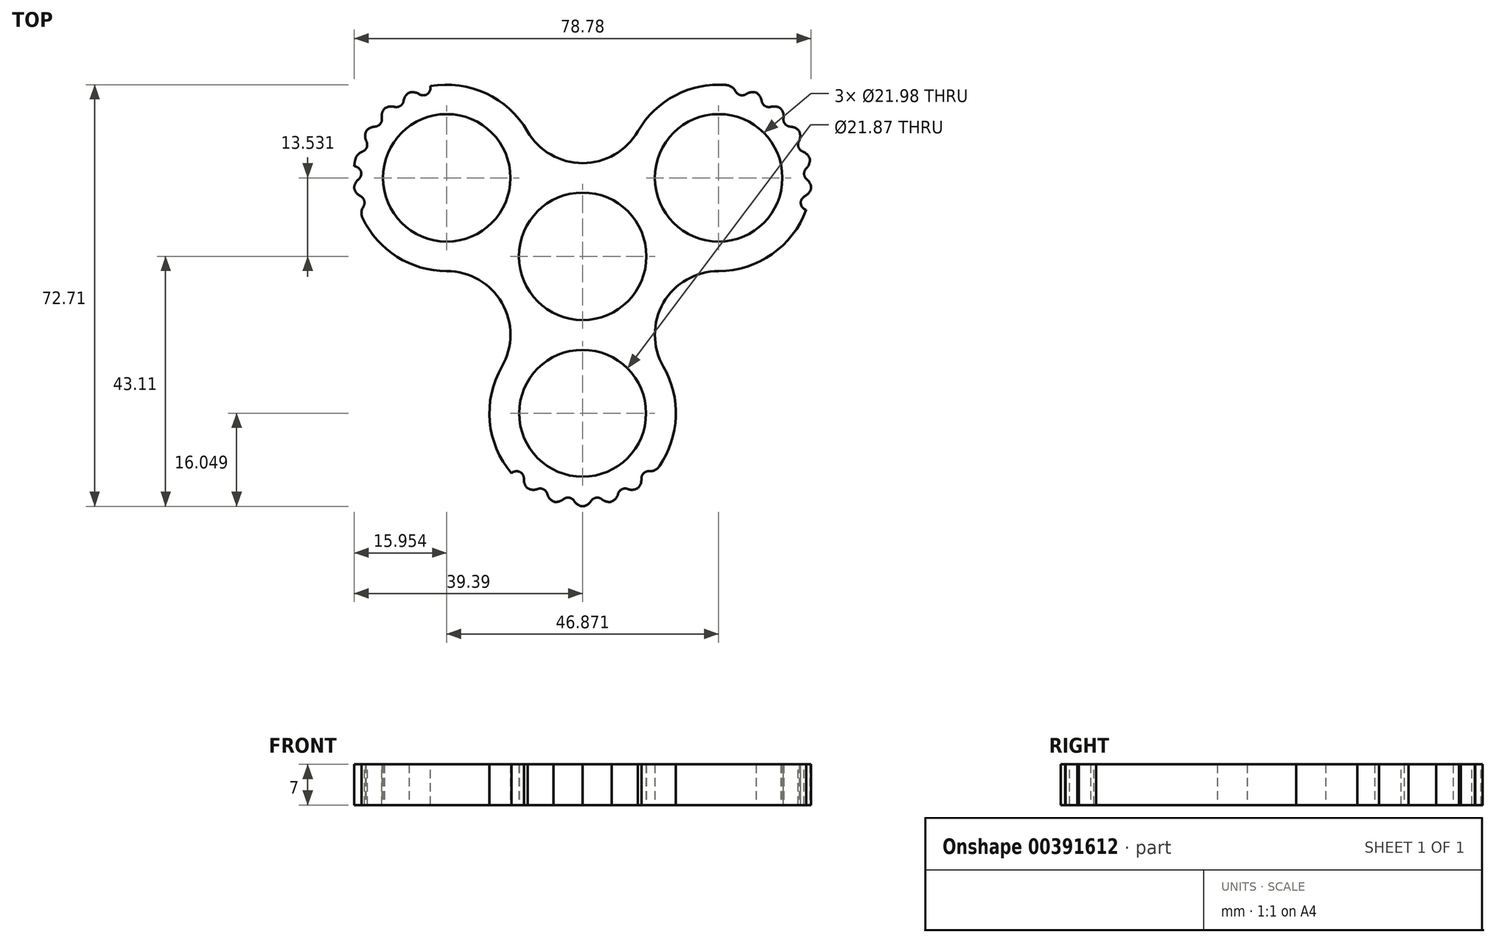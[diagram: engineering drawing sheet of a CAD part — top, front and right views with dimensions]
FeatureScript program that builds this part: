
annotation { "Feature Type Name" : "Feature", "Feature Type Description" : "" }
export const myFeature = defineFeature(function(context is Context, id is Id, definition is map)
    precondition{}
    {
        {
            var Q0;
            Q0=qCreatedBy(makeId("Top.planeOp"),FACE);
            var sketch = newSketch(context, id + "F0", { "sketchPlane" : qUnion([Q0])});
            skArc(sketch, "E0", {"start": v(0, 11) * mm, "mid": v(-5.5, -9.52) * mm, "end": v(9.52, 5.5) * mm, "construction": true});
            skLineSegment(sketch, "E1", {"start": v(0, 0) * mm, "end": v(92.12, 53.18) * mm, "construction": true});
            skLineSegment(sketch, "E2", {"start": v(0, 0) * mm, "end": v(-9.52, 5.5) * mm, "construction": true});
            skLineSegment(sketch, "E3", {"start": v(0, 0) * mm, "end": v(0, -70.87) * mm, "construction": true});
            skCircle(sketch, "E4", {"center": v(-23.44, 13.53) * mm, "radius": 11 * mm, "construction": true});
            skArc(sketch, "E5", {"start": v(13.92, 8.04) * mm, "mid": v(28.93, 4.01) * mm, "end": v(32.95, 19.03) * mm, "construction": true});
            skCircle(sketch, "E6", {"center": v(0, -27.06) * mm, "radius": 11 * mm, "construction": true});
            skLineSegment(sketch, "E7", {"start": v(0, 0) * mm, "end": v(-69.62, -40.2) * mm, "construction": true});
            skLineSegment(sketch, "E8", {"start": v(0, 0) * mm, "end": v(71.9, -41.52) * mm, "construction": true});
            skLineSegment(sketch, "E9", {"start": v(0, 0) * mm, "end": v(0, 11) * mm, "construction": true});
            skLineSegment(sketch, "E10", {"start": v(-23.44, 13.53) * mm, "end": v(-12.14, 33.1) * mm, "construction": true});
            skLineSegment(sketch, "E11", {"start": v(23.44, 13.53) * mm, "end": v(12.02, 33.3) * mm, "construction": true});
            skLineSegment(sketch, "E12", {"start": v(-37.35, 21.57) * mm, "end": v(-32.95, 19.03) * mm, "construction": true});
            skLineSegment(sketch, "E13", {"start": v(9.52, 5.5) * mm, "end": v(13.92, 8.04) * mm});
            skLineSegment(sketch, "E14", {"start": v(37.35, 21.57) * mm, "end": v(32.95, 19.03) * mm});
            skArc(sketch, "E15", {"start": v(-9.52, 5.5) * mm, "mid": v(-5.5, 9.52) * mm, "end": v(0, 11) * mm});
            skArc(sketch, "E16", {"start": v(-9.52, 21.57) * mm, "mid": v(-5.5, 17.54) * mm, "end": v(0, 16.07) * mm});
            skArc(sketch, "E17", {"start": v(-32.95, 19.03) * mm, "mid": v(-17.94, 23.05) * mm, "end": v(-13.92, 8.04) * mm});
            skLineSegment(sketch, "E18.trimOffspring", {"start": v(-37.35, 21.57) * mm, "end": v(-92.12, 53.18) * mm, "construction": true});
            skLineSegment(sketch, "E19.trimOffspring", {"start": v(-13.92, 8.04) * mm, "end": v(-32.95, 19.03) * mm, "construction": true});
            skArc(sketch, "E20", {"start": v(-9.52, 21.57) * mm, "mid": v(-23.44, 29.6) * mm, "end": v(-37.35, 21.57) * mm});
            skLineSegment(sketch, "E21", {"start": v(-37.35, 21.57) * mm, "end": v(-32.95, 19.03) * mm});
            skLineSegment(sketch, "E22", {"start": v(-13.92, 8.04) * mm, "end": v(-9.52, 5.5) * mm});
            skPoint(sketch, "E23.start.orphan", {"position": v(23.44, 29.6) * mm});
            skLineSegment(sketch, "E24.trimOffspring", {"start": v(0, 16.07) * mm, "end": v(0, 62.86) * mm, "construction": true});
            skLineSegment(sketch, "E25", {"start": v(0, 16.07) * mm, "end": v(0, 11) * mm});
            skLineSegment(sketch, "E26.MirrorCS", {"start": v(-13.92, -8.04) * mm, "end": v(-9.52, -5.5) * mm});
            skArc(sketch, "E27.MirrorCS", {"start": v(-23.44, -2.54) * mm, "mid": v(-17.94, -4.01) * mm, "end": v(-13.92, -8.04) * mm});
            skArc(sketch, "E28.MirrorCS", {"start": v(-23.44, -2.54) * mm, "mid": v(-37.35, 5.5) * mm, "end": v(-37.35, 21.57) * mm});
            skArc(sketch, "E29.MirrorCS", {"start": v(-9.52, 5.5) * mm, "mid": v(-11, 0) * mm, "end": v(-9.52, -5.5) * mm});
            skArc(sketch, "E30.MirrorCS", {"start": v(-32.95, 19.03) * mm, "mid": v(-28.93, 4.01) * mm, "end": v(-13.92, 8.04) * mm});
            skArc(sketch, "E31.MirrorCS", {"start": v(23.44, -2.54) * mm, "mid": v(37.35, 5.5) * mm, "end": v(37.35, 21.57) * mm});
            skLineSegment(sketch, "E32.MirrorCS", {"start": v(13.92, 8.04) * mm, "end": v(9.52, 5.5) * mm});
            skArc(sketch, "E33.MirrorCS", {"start": v(32.95, 19.03) * mm, "mid": v(17.94, 23.05) * mm, "end": v(13.92, 8.04) * mm});
            skArc(sketch, "E34.MirrorCS", {"start": v(32.95, 19.03) * mm, "mid": v(28.93, 4.01) * mm, "end": v(13.92, 8.04) * mm});
            skLineSegment(sketch, "E35.MirrorCS", {"start": v(13.92, -8.04) * mm, "end": v(9.52, -5.5) * mm});
            skArc(sketch, "E36.MirrorCS", {"start": v(23.44, -2.54) * mm, "mid": v(17.94, -4.01) * mm, "end": v(13.92, -8.04) * mm});
            skLineSegment(sketch, "E37.MirrorCS", {"start": v(37.35, 21.57) * mm, "end": v(32.95, 19.03) * mm, "construction": true});
            skArc(sketch, "E38.MirrorCS", {"start": v(9.52, 5.5) * mm, "mid": v(11, 0) * mm, "end": v(9.52, -5.5) * mm});
            skArc(sketch, "E39.MirrorCS", {"start": v(9.52, 21.57) * mm, "mid": v(23.44, 29.6) * mm, "end": v(37.35, 21.57) * mm});
            skLineSegment(sketch, "E40.MirrorCS", {"start": v(23.44, 13.53) * mm, "end": v(12.14, 33.1) * mm, "construction": true});
            skLineSegment(sketch, "E41.MirrorCS", {"start": v(0, 0) * mm, "end": v(9.52, 5.5) * mm, "construction": true});
            skArc(sketch, "E42.MirrorCS", {"start": v(9.52, 5.5) * mm, "mid": v(5.5, 9.52) * mm, "end": v(0, 11) * mm});
            skArc(sketch, "E43.MirrorCS", {"start": v(9.52, 21.57) * mm, "mid": v(5.5, 17.54) * mm, "end": v(0, 16.07) * mm});
            skCircle(sketch, "E44.MirrorC", {"center": v(23.44, 13.53) * mm, "radius": 11 * mm, "construction": true});
            skLineSegment(sketch, "E45.MirrorCS", {"start": v(13.92, 8.04) * mm, "end": v(32.95, 19.03) * mm, "construction": true});
            skArc(sketch, "E46", {"start": v(-9.52, -5.5) * mm, "mid": v(0, -11) * mm, "end": v(9.52, -5.5) * mm});
            skArc(sketch, "E47.MirrorCS", {"start": v(-13.92, -19.03) * mm, "mid": v(-12.45, -13.53) * mm, "end": v(-13.92, -8.04) * mm});
            skArc(sketch, "E48.MirrorCS", {"start": v(-13.92, -19.03) * mm, "mid": v(-13.92, -35.1) * mm, "end": v(0, -43.13) * mm});
            skArc(sketch, "E49.MirrorCS", {"start": v(13.92, -19.03) * mm, "mid": v(12.45, -13.53) * mm, "end": v(13.92, -8.04) * mm});
            skArc(sketch, "E50.MirrorCS", {"start": v(13.92, -19.03) * mm, "mid": v(13.92, -35.1) * mm, "end": v(0, -43.13) * mm});
            skCircle(sketch, "E51", {"center": v(0, -27.06) * mm, "radius": 10.94 * mm});
            skSolve(sketch);
        }
        {
            var Q0;
            Q0=qSketchRegion(id+"F0",true);
            extrude(context, id + "F1", {"entities" : qUnion([Q0]), "depth" : 7 * mm});
        }
        {
            var Q0;
            Q0=makeQuery(id+"F1.opExtrude","CAP_FACE",FACE,{"disambiguationData":[OSD([sQuery(id+"F0.wireOp",EDGE,"E15"),sQuery(id+"F0.wireOp",EDGE,"E16"),sQuery(id+"F0.wireOp",EDGE,"E17"),sQuery(id+"F0.wireOp",EDGE,"E20"),sQuery(id+"F0.wireOp",EDGE,"E27.MirrorCS"),sQuery(id+"F0.wireOp",EDGE,"E29.MirrorCS"),sQuery(id+"F0.wireOp",EDGE,"E30.MirrorCS"),sQuery(id+"F0.wireOp",EDGE,"E28.MirrorCS"),sQuery(id+"F0.wireOp",EDGE,"E33.MirrorCS"),sQuery(id+"F0.wireOp",EDGE,"E34.MirrorCS"),sQuery(id+"F0.wireOp",EDGE,"E31.MirrorCS"),sQuery(id+"F0.wireOp",EDGE,"E36.MirrorCS"),sQuery(id+"F0.wireOp",EDGE,"E38.MirrorCS"),sQuery(id+"F0.wireOp",EDGE,"E39.MirrorCS"),sQuery(id+"F0.wireOp",EDGE,"E42.MirrorCS"),sQuery(id+"F0.wireOp",EDGE,"E43.MirrorCS"),sQuery(id+"F0.wireOp",EDGE,"E46"),sQuery(id+"F0.wireOp",EDGE,"E47.MirrorCS"),sQuery(id+"F0.wireOp",EDGE,"E48.MirrorCS"),sQuery(id+"F0.wireOp",EDGE,"E49.MirrorCS"),sQuery(id+"F0.wireOp",EDGE,"E50.MirrorCS"),sQuery(id+"F0.wireOp",EDGE,"E51")])],"isStart":false});
            var sketch = newSketch(context, id + "F2", { "sketchPlane" : qUnion([Q0])});
            skArc(sketch, "E52", {"start": v(-36.68, 22.64) * mm, "mid": v(-34.89, 22.83) * mm, "end": v(-35.07, 24.61) * mm});
            skArc(sketch, "E53", {"start": v(-38.85, 18.07) * mm, "mid": v(-37.21, 18.8) * mm, "end": v(-37.94, 20.44) * mm});
            skArc(sketch, "E54", {"start": v(-36.68, 22.64) * mm, "mid": v(-35.91, 23.66) * mm, "end": v(-35.07, 24.61) * mm});
            skArc(sketch, "E55", {"start": v(-38.85, 18.07) * mm, "mid": v(-38.45, 19.27) * mm, "end": v(-37.94, 20.44) * mm});
            skArc(sketch, "E56", {"start": v(-39.5, 12.99) * mm, "mid": v(-38.17, 14.2) * mm, "end": v(-39.38, 15.53) * mm});
            skArc(sketch, "E57", {"start": v(-33.18, 26.3) * mm, "mid": v(-31.43, 25.93) * mm, "end": v(-31.05, 27.68) * mm});
            skArc(sketch, "E58", {"start": v(-33.18, 26.3) * mm, "mid": v(-32.14, 27.04) * mm, "end": v(-31.05, 27.68) * mm});
            skArc(sketch, "E59", {"start": v(-39.5, 12.99) * mm, "mid": v(-39.49, 14.26) * mm, "end": v(-39.38, 15.53) * mm});
            skArc(sketch, "E60", {"start": v(-38.53, 8.02) * mm, "mid": v(-37.65, 9.58) * mm, "end": v(-39.21, 10.47) * mm});
            skArc(sketch, "E61", {"start": v(-28.72, 28.7) * mm, "mid": v(-27.17, 27.8) * mm, "end": v(-26.27, 29.35) * mm});
            skArc(sketch, "E62", {"start": v(-28.72, 28.7) * mm, "mid": v(-27.5, 29.08) * mm, "end": v(-26.27, 29.35) * mm});
            skArc(sketch, "E63", {"start": v(-38.53, 8.02) * mm, "mid": v(-38.92, 9.23) * mm, "end": v(-39.21, 10.47) * mm});
            skLineSegment(sketch, "E64", {"start": v(0, 53.35) * mm, "end": v(0, -27.06) * mm, "construction": true});
            skArc(sketch, "E65.MirrorCS", {"start": v(28.72, 28.7) * mm, "mid": v(27.17, 27.8) * mm, "end": v(26.27, 29.35) * mm});
            skArc(sketch, "E66.MirrorCS", {"start": v(28.72, 28.7) * mm, "mid": v(27.5, 29.08) * mm, "end": v(26.27, 29.35) * mm});
            skArc(sketch, "E67.MirrorCS", {"start": v(33.18, 26.3) * mm, "mid": v(31.43, 25.93) * mm, "end": v(31.05, 27.68) * mm});
            skArc(sketch, "E68.MirrorCS", {"start": v(33.18, 26.3) * mm, "mid": v(32.14, 27.04) * mm, "end": v(31.05, 27.68) * mm});
            skArc(sketch, "E69.MirrorCS", {"start": v(36.68, 22.64) * mm, "mid": v(34.89, 22.83) * mm, "end": v(35.07, 24.61) * mm});
            skArc(sketch, "E70.MirrorCS", {"start": v(38.85, 18.07) * mm, "mid": v(37.21, 18.8) * mm, "end": v(37.94, 20.44) * mm});
            skArc(sketch, "E71.MirrorCS", {"start": v(39.5, 12.99) * mm, "mid": v(38.17, 14.2) * mm, "end": v(39.38, 15.53) * mm});
            skArc(sketch, "E72.MirrorCS", {"start": v(38.53, 8.02) * mm, "mid": v(37.65, 9.58) * mm, "end": v(39.21, 10.47) * mm});
            skArc(sketch, "E73.MirrorCS", {"start": v(36.68, 22.64) * mm, "mid": v(35.91, 23.66) * mm, "end": v(35.07, 24.61) * mm});
            skArc(sketch, "E74.MirrorCS", {"start": v(38.85, 18.07) * mm, "mid": v(38.45, 19.27) * mm, "end": v(37.94, 20.44) * mm});
            skArc(sketch, "E75.MirrorCS", {"start": v(39.5, 12.99) * mm, "mid": v(39.49, 14.26) * mm, "end": v(39.38, 15.53) * mm});
            skArc(sketch, "E76.MirrorCS", {"start": v(38.53, 8.02) * mm, "mid": v(38.92, 9.23) * mm, "end": v(39.21, 10.47) * mm});
            skArc(sketch, "E77", {"start": v(3.78, -42.68) * mm, "mid": v(2.32, -41.63) * mm, "end": v(1.27, -43.08) * mm});
            skArc(sketch, "E78", {"start": v(8.45, -40.73) * mm, "mid": v(6.74, -40.18) * mm, "end": v(6.2, -41.9) * mm});
            skArc(sketch, "E79", {"start": v(12.28, -37.42) * mm, "mid": v(10.49, -37.43) * mm, "end": v(10.5, -39.23) * mm});
            skArc(sketch, "E80", {"start": v(-1.27, -43.08) * mm, "mid": v(-2.32, -41.63) * mm, "end": v(-3.78, -42.68) * mm});
            skArc(sketch, "E81", {"start": v(-6.2, -41.9) * mm, "mid": v(-6.74, -40.18) * mm, "end": v(-8.45, -40.73) * mm});
            skArc(sketch, "E82", {"start": v(-10.5, -39.23) * mm, "mid": v(-10.49, -37.43) * mm, "end": v(-12.28, -37.42) * mm});
            skArc(sketch, "E83", {"start": v(12.28, -37.42) * mm, "mid": v(11.43, -38.36) * mm, "end": v(10.5, -39.23) * mm});
            skArc(sketch, "E84", {"start": v(8.45, -40.73) * mm, "mid": v(7.34, -41.36) * mm, "end": v(6.2, -41.9) * mm});
            skArc(sketch, "E85", {"start": v(3.78, -42.68) * mm, "mid": v(2.53, -42.93) * mm, "end": v(1.27, -43.08) * mm});
            skArc(sketch, "E86", {"start": v(-1.27, -43.08) * mm, "mid": v(-2.53, -42.93) * mm, "end": v(-3.78, -42.68) * mm});
            skArc(sketch, "E87", {"start": v(-6.2, -41.9) * mm, "mid": v(-7.34, -41.36) * mm, "end": v(-8.45, -40.73) * mm});
            skArc(sketch, "E88", {"start": v(-10.5, -39.23) * mm, "mid": v(-11.43, -38.36) * mm, "end": v(-12.28, -37.42) * mm});
            skSolve(sketch);
        }
        {
            var Q0;
            Q0=qSketchRegion(id+"F2",true);
            extrude(context, id + "F3", {"entities" : qUnion([Q0]), "operationType" : NewBodyOperationType.REMOVE, "endBound" : BoundingType.THROUGH_ALL, "oppositeDirection" : true, "depth" : 25.4 * mm});
        }
        {
            var Q0;
            {var subQ0=sQuery(id+"F2.wireOp",EDGE,"E84");var subQ1=sQuery(id+"F2.wireOp",EDGE,"E78");var subQ2=sQuery(id+"F0.wireOp",EDGE,"E50.MirrorCS");var subQ3=sQuery(id+"F0.wireOp",EDGE,"E48.MirrorCS");Q0=makeQuery(id+"F3.boolean.opBoolean","COPY",EDGE,{"derivedFrom":makeQuery(id+"F3.opExtrude","SWEPT_EDGE",EDGE,{"disambiguationData":[OSD([subQ3,subQ2,subQ1,subQ0]),TDD([makeQuery(id+"F2.imprint","INTERSECT",VERTEX,{"disambiguationData":[OD(0.0)],"derivedFrom":[makeQuery(id+"F1.opExtrude","CAP_EDGE",EDGE,{"disambiguationData":[OSD([subQ3,subQ2])],"isStart":false}),subQ1,subQ0]})])]})});}
            var Q1;
            {var subQ0=sQuery(id+"F2.wireOp",EDGE,"E83");var subQ1=sQuery(id+"F2.wireOp",EDGE,"E79");var subQ2=sQuery(id+"F0.wireOp",EDGE,"E50.MirrorCS");var subQ3=sQuery(id+"F0.wireOp",EDGE,"E48.MirrorCS");Q1=makeQuery(id+"F3.boolean.opBoolean","COPY",EDGE,{"derivedFrom":makeQuery(id+"F3.opExtrude","SWEPT_EDGE",EDGE,{"disambiguationData":[OSD([subQ3,subQ2,subQ1,subQ0]),TDD([makeQuery(id+"F2.imprint","INTERSECT",VERTEX,{"disambiguationData":[OD(1.0)],"derivedFrom":[makeQuery(id+"F1.opExtrude","CAP_EDGE",EDGE,{"disambiguationData":[OSD([subQ3,subQ2])],"isStart":false}),subQ1,subQ0]})])]})});}
            var Q2;
            {var subQ0=sQuery(id+"F2.wireOp",EDGE,"E85");var subQ1=sQuery(id+"F2.wireOp",EDGE,"E77");var subQ2=sQuery(id+"F0.wireOp",EDGE,"E50.MirrorCS");var subQ3=sQuery(id+"F0.wireOp",EDGE,"E48.MirrorCS");Q2=makeQuery(id+"F3.boolean.opBoolean","COPY",EDGE,{"derivedFrom":makeQuery(id+"F3.opExtrude","SWEPT_EDGE",EDGE,{"disambiguationData":[OSD([subQ3,subQ2,subQ1,subQ0]),TDD([makeQuery(id+"F2.imprint","INTERSECT",VERTEX,{"disambiguationData":[OD(0.0)],"derivedFrom":[makeQuery(id+"F1.opExtrude","CAP_EDGE",EDGE,{"disambiguationData":[OSD([subQ3,subQ2])],"isStart":false}),subQ1,subQ0]})])]})});}
            var Q3;
            {var subQ0=sQuery(id+"F2.wireOp",EDGE,"E84");var subQ1=sQuery(id+"F2.wireOp",EDGE,"E78");var subQ2=sQuery(id+"F0.wireOp",EDGE,"E50.MirrorCS");var subQ3=sQuery(id+"F0.wireOp",EDGE,"E48.MirrorCS");Q3=makeQuery(id+"F3.boolean.opBoolean","COPY",EDGE,{"derivedFrom":makeQuery(id+"F3.opExtrude","SWEPT_EDGE",EDGE,{"disambiguationData":[OSD([subQ3,subQ2,subQ1,subQ0]),TDD([makeQuery(id+"F2.imprint","INTERSECT",VERTEX,{"disambiguationData":[OD(1.0)],"derivedFrom":[makeQuery(id+"F1.opExtrude","CAP_EDGE",EDGE,{"disambiguationData":[OSD([subQ3,subQ2])],"isStart":false}),subQ1,subQ0]})])]})});}
            var Q4;
            {var subQ0=sQuery(id+"F2.wireOp",EDGE,"E85");var subQ1=sQuery(id+"F2.wireOp",EDGE,"E77");var subQ2=sQuery(id+"F0.wireOp",EDGE,"E50.MirrorCS");var subQ3=sQuery(id+"F0.wireOp",EDGE,"E48.MirrorCS");Q4=makeQuery(id+"F3.boolean.opBoolean","COPY",EDGE,{"derivedFrom":makeQuery(id+"F3.opExtrude","SWEPT_EDGE",EDGE,{"disambiguationData":[OSD([subQ3,subQ2,subQ1,subQ0]),TDD([makeQuery(id+"F2.imprint","INTERSECT",VERTEX,{"disambiguationData":[OD(1.0)],"derivedFrom":[makeQuery(id+"F1.opExtrude","CAP_EDGE",EDGE,{"disambiguationData":[OSD([subQ3,subQ2])],"isStart":false}),subQ1,subQ0]})])]})});}
            var Q5;
            {var subQ0=sQuery(id+"F2.wireOp",EDGE,"E86");var subQ1=sQuery(id+"F2.wireOp",EDGE,"E80");var subQ2=sQuery(id+"F0.wireOp",EDGE,"E50.MirrorCS");var subQ3=sQuery(id+"F0.wireOp",EDGE,"E48.MirrorCS");Q5=makeQuery(id+"F3.boolean.opBoolean","COPY",EDGE,{"derivedFrom":makeQuery(id+"F3.opExtrude","SWEPT_EDGE",EDGE,{"disambiguationData":[OSD([subQ3,subQ2,subQ1,subQ0]),TDD([makeQuery(id+"F2.imprint","INTERSECT",VERTEX,{"disambiguationData":[OD(0.0)],"derivedFrom":[makeQuery(id+"F1.opExtrude","CAP_EDGE",EDGE,{"disambiguationData":[OSD([subQ3,subQ2])],"isStart":false}),subQ1,subQ0]})])]})});}
            var Q6;
            {var subQ0=sQuery(id+"F2.wireOp",EDGE,"E86");var subQ1=sQuery(id+"F2.wireOp",EDGE,"E80");var subQ2=sQuery(id+"F0.wireOp",EDGE,"E50.MirrorCS");var subQ3=sQuery(id+"F0.wireOp",EDGE,"E48.MirrorCS");Q6=makeQuery(id+"F3.boolean.opBoolean","COPY",EDGE,{"derivedFrom":makeQuery(id+"F3.opExtrude","SWEPT_EDGE",EDGE,{"disambiguationData":[OSD([subQ3,subQ2,subQ1,subQ0]),TDD([makeQuery(id+"F2.imprint","INTERSECT",VERTEX,{"disambiguationData":[OD(1.0)],"derivedFrom":[makeQuery(id+"F1.opExtrude","CAP_EDGE",EDGE,{"disambiguationData":[OSD([subQ3,subQ2])],"isStart":false}),subQ1,subQ0]})])]})});}
            var Q7;
            {var subQ0=sQuery(id+"F2.wireOp",EDGE,"E87");var subQ1=sQuery(id+"F2.wireOp",EDGE,"E81");var subQ2=sQuery(id+"F0.wireOp",EDGE,"E50.MirrorCS");var subQ3=sQuery(id+"F0.wireOp",EDGE,"E48.MirrorCS");Q7=makeQuery(id+"F3.boolean.opBoolean","COPY",EDGE,{"derivedFrom":makeQuery(id+"F3.opExtrude","SWEPT_EDGE",EDGE,{"disambiguationData":[OSD([subQ3,subQ2,subQ1,subQ0]),TDD([makeQuery(id+"F2.imprint","INTERSECT",VERTEX,{"disambiguationData":[OD(0.0)],"derivedFrom":[makeQuery(id+"F1.opExtrude","CAP_EDGE",EDGE,{"disambiguationData":[OSD([subQ3,subQ2])],"isStart":false}),subQ1,subQ0]})])]})});}
            var Q8;
            {var subQ0=sQuery(id+"F2.wireOp",EDGE,"E87");var subQ1=sQuery(id+"F2.wireOp",EDGE,"E81");var subQ2=sQuery(id+"F0.wireOp",EDGE,"E50.MirrorCS");var subQ3=sQuery(id+"F0.wireOp",EDGE,"E48.MirrorCS");Q8=makeQuery(id+"F3.boolean.opBoolean","COPY",EDGE,{"derivedFrom":makeQuery(id+"F3.opExtrude","SWEPT_EDGE",EDGE,{"disambiguationData":[OSD([subQ3,subQ2,subQ1,subQ0]),TDD([makeQuery(id+"F2.imprint","INTERSECT",VERTEX,{"disambiguationData":[OD(1.0)],"derivedFrom":[makeQuery(id+"F1.opExtrude","CAP_EDGE",EDGE,{"disambiguationData":[OSD([subQ3,subQ2])],"isStart":false}),subQ1,subQ0]})])]})});}
            var Q9;
            {var subQ0=sQuery(id+"F2.wireOp",EDGE,"E88");var subQ1=sQuery(id+"F2.wireOp",EDGE,"E82");var subQ2=sQuery(id+"F0.wireOp",EDGE,"E50.MirrorCS");var subQ3=sQuery(id+"F0.wireOp",EDGE,"E48.MirrorCS");Q9=makeQuery(id+"F3.boolean.opBoolean","COPY",EDGE,{"derivedFrom":makeQuery(id+"F3.opExtrude","SWEPT_EDGE",EDGE,{"disambiguationData":[OSD([subQ3,subQ2,subQ1,subQ0]),TDD([makeQuery(id+"F2.imprint","INTERSECT",VERTEX,{"disambiguationData":[OD(0.0)],"derivedFrom":[makeQuery(id+"F1.opExtrude","CAP_EDGE",EDGE,{"disambiguationData":[OSD([subQ3,subQ2])],"isStart":false}),subQ1,subQ0]})])]})});}
            var Q10;
            {var subQ0=sQuery(id+"F2.wireOp",EDGE,"E62");var subQ1=sQuery(id+"F2.wireOp",EDGE,"E61");var subQ2=sQuery(id+"F0.wireOp",EDGE,"E28.MirrorCS");var subQ3=sQuery(id+"F0.wireOp",EDGE,"E20");Q10=makeQuery(id+"F3.boolean.opBoolean","COPY",EDGE,{"derivedFrom":makeQuery(id+"F3.opExtrude","SWEPT_EDGE",EDGE,{"disambiguationData":[OSD([subQ3,subQ2,subQ1,subQ0]),TDD([makeQuery(id+"F2.imprint","INTERSECT",VERTEX,{"disambiguationData":[OD(0.0)],"derivedFrom":[makeQuery(id+"F1.opExtrude","CAP_EDGE",EDGE,{"disambiguationData":[OSD([subQ3,subQ2])],"isStart":false}),subQ1,subQ0]})])]})});}
            var Q11;
            {var subQ0=sQuery(id+"F2.wireOp",EDGE,"E58");var subQ1=sQuery(id+"F2.wireOp",EDGE,"E57");var subQ2=sQuery(id+"F0.wireOp",EDGE,"E28.MirrorCS");var subQ3=sQuery(id+"F0.wireOp",EDGE,"E20");Q11=makeQuery(id+"F3.boolean.opBoolean","COPY",EDGE,{"derivedFrom":makeQuery(id+"F3.opExtrude","SWEPT_EDGE",EDGE,{"disambiguationData":[OSD([subQ3,subQ2,subQ1,subQ0]),TDD([makeQuery(id+"F2.imprint","INTERSECT",VERTEX,{"disambiguationData":[OD(1.0)],"derivedFrom":[makeQuery(id+"F1.opExtrude","CAP_EDGE",EDGE,{"disambiguationData":[OSD([subQ3,subQ2])],"isStart":false}),subQ1,subQ0]})])]})});}
            var Q12;
            {var subQ0=sQuery(id+"F2.wireOp",EDGE,"E58");var subQ1=sQuery(id+"F2.wireOp",EDGE,"E57");var subQ2=sQuery(id+"F0.wireOp",EDGE,"E28.MirrorCS");var subQ3=sQuery(id+"F0.wireOp",EDGE,"E20");Q12=makeQuery(id+"F3.boolean.opBoolean","COPY",EDGE,{"derivedFrom":makeQuery(id+"F3.opExtrude","SWEPT_EDGE",EDGE,{"disambiguationData":[OSD([subQ3,subQ2,subQ1,subQ0]),TDD([makeQuery(id+"F2.imprint","INTERSECT",VERTEX,{"disambiguationData":[OD(0.0)],"derivedFrom":[makeQuery(id+"F1.opExtrude","CAP_EDGE",EDGE,{"disambiguationData":[OSD([subQ3,subQ2])],"isStart":false}),subQ1,subQ0]})])]})});}
            var Q13;
            {var subQ0=sQuery(id+"F2.wireOp",EDGE,"E54");var subQ1=sQuery(id+"F2.wireOp",EDGE,"E52");var subQ2=sQuery(id+"F0.wireOp",EDGE,"E28.MirrorCS");var subQ3=sQuery(id+"F0.wireOp",EDGE,"E20");Q13=makeQuery(id+"F3.boolean.opBoolean","COPY",EDGE,{"derivedFrom":makeQuery(id+"F3.opExtrude","SWEPT_EDGE",EDGE,{"disambiguationData":[OSD([subQ3,subQ2,subQ1,subQ0]),TDD([makeQuery(id+"F2.imprint","INTERSECT",VERTEX,{"disambiguationData":[OD(1.0)],"derivedFrom":[makeQuery(id+"F1.opExtrude","CAP_EDGE",EDGE,{"disambiguationData":[OSD([subQ3,subQ2])],"isStart":false}),subQ1,subQ0]})])]})});}
            var Q14;
            {var subQ0=sQuery(id+"F2.wireOp",EDGE,"E54");var subQ1=sQuery(id+"F2.wireOp",EDGE,"E52");var subQ2=sQuery(id+"F0.wireOp",EDGE,"E28.MirrorCS");var subQ3=sQuery(id+"F0.wireOp",EDGE,"E20");Q14=makeQuery(id+"F3.boolean.opBoolean","COPY",EDGE,{"derivedFrom":makeQuery(id+"F3.opExtrude","SWEPT_EDGE",EDGE,{"disambiguationData":[OSD([subQ3,subQ2,subQ1,subQ0]),TDD([makeQuery(id+"F2.imprint","INTERSECT",VERTEX,{"disambiguationData":[OD(0.0)],"derivedFrom":[makeQuery(id+"F1.opExtrude","CAP_EDGE",EDGE,{"disambiguationData":[OSD([subQ3,subQ2])],"isStart":false}),subQ1,subQ0]})])]})});}
            var Q15;
            {var subQ0=sQuery(id+"F2.wireOp",EDGE,"E55");var subQ1=sQuery(id+"F2.wireOp",EDGE,"E53");var subQ2=sQuery(id+"F0.wireOp",EDGE,"E28.MirrorCS");var subQ3=sQuery(id+"F0.wireOp",EDGE,"E20");Q15=makeQuery(id+"F3.boolean.opBoolean","COPY",EDGE,{"derivedFrom":makeQuery(id+"F3.opExtrude","SWEPT_EDGE",EDGE,{"disambiguationData":[OSD([subQ3,subQ2,subQ1,subQ0]),TDD([makeQuery(id+"F2.imprint","INTERSECT",VERTEX,{"disambiguationData":[OD(1.0)],"derivedFrom":[makeQuery(id+"F1.opExtrude","CAP_EDGE",EDGE,{"disambiguationData":[OSD([subQ3,subQ2])],"isStart":false}),subQ1,subQ0]})])]})});}
            var Q16;
            {var subQ0=sQuery(id+"F2.wireOp",EDGE,"E55");var subQ1=sQuery(id+"F2.wireOp",EDGE,"E53");var subQ2=sQuery(id+"F0.wireOp",EDGE,"E28.MirrorCS");var subQ3=sQuery(id+"F0.wireOp",EDGE,"E20");Q16=makeQuery(id+"F3.boolean.opBoolean","COPY",EDGE,{"derivedFrom":makeQuery(id+"F3.opExtrude","SWEPT_EDGE",EDGE,{"disambiguationData":[OSD([subQ3,subQ2,subQ1,subQ0]),TDD([makeQuery(id+"F2.imprint","INTERSECT",VERTEX,{"disambiguationData":[OD(0.0)],"derivedFrom":[makeQuery(id+"F1.opExtrude","CAP_EDGE",EDGE,{"disambiguationData":[OSD([subQ3,subQ2])],"isStart":false}),subQ1,subQ0]})])]})});}
            var Q17;
            {var subQ0=sQuery(id+"F2.wireOp",EDGE,"E59");var subQ1=sQuery(id+"F2.wireOp",EDGE,"E56");var subQ2=sQuery(id+"F0.wireOp",EDGE,"E28.MirrorCS");var subQ3=sQuery(id+"F0.wireOp",EDGE,"E20");Q17=makeQuery(id+"F3.boolean.opBoolean","COPY",EDGE,{"derivedFrom":makeQuery(id+"F3.opExtrude","SWEPT_EDGE",EDGE,{"disambiguationData":[OSD([subQ3,subQ2,subQ1,subQ0]),TDD([makeQuery(id+"F2.imprint","INTERSECT",VERTEX,{"disambiguationData":[OD(0.0)],"derivedFrom":[makeQuery(id+"F1.opExtrude","CAP_EDGE",EDGE,{"disambiguationData":[OSD([subQ3,subQ2])],"isStart":false}),subQ1,subQ0]})])]})});}
            var Q18;
            {var subQ0=sQuery(id+"F2.wireOp",EDGE,"E63");var subQ1=sQuery(id+"F2.wireOp",EDGE,"E60");var subQ2=sQuery(id+"F0.wireOp",EDGE,"E28.MirrorCS");var subQ3=sQuery(id+"F0.wireOp",EDGE,"E20");Q18=makeQuery(id+"F3.boolean.opBoolean","COPY",EDGE,{"derivedFrom":makeQuery(id+"F3.opExtrude","SWEPT_EDGE",EDGE,{"disambiguationData":[OSD([subQ3,subQ2,subQ1,subQ0]),TDD([makeQuery(id+"F2.imprint","INTERSECT",VERTEX,{"disambiguationData":[OD(1.0)],"derivedFrom":[makeQuery(id+"F1.opExtrude","CAP_EDGE",EDGE,{"disambiguationData":[OSD([subQ3,subQ2])],"isStart":false}),subQ1,subQ0]})])]})});}
            var Q19;
            {var subQ0=sQuery(id+"F2.wireOp",EDGE,"E63");var subQ1=sQuery(id+"F2.wireOp",EDGE,"E60");var subQ2=sQuery(id+"F0.wireOp",EDGE,"E28.MirrorCS");var subQ3=sQuery(id+"F0.wireOp",EDGE,"E20");Q19=makeQuery(id+"F3.boolean.opBoolean","COPY",EDGE,{"derivedFrom":makeQuery(id+"F3.opExtrude","SWEPT_EDGE",EDGE,{"disambiguationData":[OSD([subQ3,subQ2,subQ1,subQ0]),TDD([makeQuery(id+"F2.imprint","INTERSECT",VERTEX,{"disambiguationData":[OD(0.0)],"derivedFrom":[makeQuery(id+"F1.opExtrude","CAP_EDGE",EDGE,{"disambiguationData":[OSD([subQ3,subQ2])],"isStart":false}),subQ1,subQ0]})])]})});}
            var Q20;
            {var subQ0=sQuery(id+"F2.wireOp",EDGE,"E62");var subQ1=sQuery(id+"F2.wireOp",EDGE,"E61");var subQ2=sQuery(id+"F0.wireOp",EDGE,"E28.MirrorCS");var subQ3=sQuery(id+"F0.wireOp",EDGE,"E20");Q20=makeQuery(id+"F3.boolean.opBoolean","COPY",EDGE,{"derivedFrom":makeQuery(id+"F3.opExtrude","SWEPT_EDGE",EDGE,{"disambiguationData":[OSD([subQ3,subQ2,subQ1,subQ0]),TDD([makeQuery(id+"F2.imprint","INTERSECT",VERTEX,{"disambiguationData":[OD(1.0)],"derivedFrom":[makeQuery(id+"F1.opExtrude","CAP_EDGE",EDGE,{"disambiguationData":[OSD([subQ3,subQ2])],"isStart":false}),subQ1,subQ0]})])]})});}
            var Q21;
            {var subQ0=sQuery(id+"F2.wireOp",EDGE,"E88");var subQ1=sQuery(id+"F2.wireOp",EDGE,"E82");var subQ2=sQuery(id+"F0.wireOp",EDGE,"E50.MirrorCS");var subQ3=sQuery(id+"F0.wireOp",EDGE,"E48.MirrorCS");Q21=makeQuery(id+"F3.boolean.opBoolean","COPY",EDGE,{"derivedFrom":makeQuery(id+"F3.opExtrude","SWEPT_EDGE",EDGE,{"disambiguationData":[OSD([subQ3,subQ2,subQ1,subQ0]),TDD([makeQuery(id+"F2.imprint","INTERSECT",VERTEX,{"disambiguationData":[OD(1.0)],"derivedFrom":[makeQuery(id+"F1.opExtrude","CAP_EDGE",EDGE,{"disambiguationData":[OSD([subQ3,subQ2])],"isStart":false}),subQ1,subQ0]})])]})});}
            var Q22;
            {var subQ0=sQuery(id+"F2.wireOp",EDGE,"E83");var subQ1=sQuery(id+"F2.wireOp",EDGE,"E79");var subQ2=sQuery(id+"F0.wireOp",EDGE,"E50.MirrorCS");var subQ3=sQuery(id+"F0.wireOp",EDGE,"E48.MirrorCS");Q22=makeQuery(id+"F3.boolean.opBoolean","COPY",EDGE,{"derivedFrom":makeQuery(id+"F3.opExtrude","SWEPT_EDGE",EDGE,{"disambiguationData":[OSD([subQ3,subQ2,subQ1,subQ0]),TDD([makeQuery(id+"F2.imprint","INTERSECT",VERTEX,{"disambiguationData":[OD(0.0)],"derivedFrom":[makeQuery(id+"F1.opExtrude","CAP_EDGE",EDGE,{"disambiguationData":[OSD([subQ3,subQ2])],"isStart":false}),subQ1,subQ0]})])]})});}
            var Q23;
            {var subQ0=sQuery(id+"F2.wireOp",EDGE,"E66.MirrorCS");var subQ1=sQuery(id+"F2.wireOp",EDGE,"E65.MirrorCS");var subQ2=sQuery(id+"F0.wireOp",EDGE,"E39.MirrorCS");var subQ3=sQuery(id+"F0.wireOp",EDGE,"E31.MirrorCS");Q23=makeQuery(id+"F3.boolean.opBoolean","COPY",EDGE,{"derivedFrom":makeQuery(id+"F3.opExtrude","SWEPT_EDGE",EDGE,{"disambiguationData":[OSD([subQ3,subQ2,subQ1,subQ0]),TDD([makeQuery(id+"F2.imprint","INTERSECT",VERTEX,{"disambiguationData":[OD(1.0)],"derivedFrom":[makeQuery(id+"F1.opExtrude","CAP_EDGE",EDGE,{"disambiguationData":[OSD([subQ3,subQ2])],"isStart":false}),subQ1,subQ0]})])]})});}
            var Q24;
            {var subQ0=sQuery(id+"F2.wireOp",EDGE,"E66.MirrorCS");var subQ1=sQuery(id+"F2.wireOp",EDGE,"E65.MirrorCS");var subQ2=sQuery(id+"F0.wireOp",EDGE,"E39.MirrorCS");var subQ3=sQuery(id+"F0.wireOp",EDGE,"E31.MirrorCS");Q24=makeQuery(id+"F3.boolean.opBoolean","COPY",EDGE,{"derivedFrom":makeQuery(id+"F3.opExtrude","SWEPT_EDGE",EDGE,{"disambiguationData":[OSD([subQ3,subQ2,subQ1,subQ0]),TDD([makeQuery(id+"F2.imprint","INTERSECT",VERTEX,{"disambiguationData":[OD(0.0)],"derivedFrom":[makeQuery(id+"F1.opExtrude","CAP_EDGE",EDGE,{"disambiguationData":[OSD([subQ3,subQ2])],"isStart":false}),subQ1,subQ0]})])]})});}
            var Q25;
            {var subQ0=sQuery(id+"F2.wireOp",EDGE,"E68.MirrorCS");var subQ1=sQuery(id+"F2.wireOp",EDGE,"E67.MirrorCS");var subQ2=sQuery(id+"F0.wireOp",EDGE,"E39.MirrorCS");var subQ3=sQuery(id+"F0.wireOp",EDGE,"E31.MirrorCS");Q25=makeQuery(id+"F3.boolean.opBoolean","COPY",EDGE,{"derivedFrom":makeQuery(id+"F3.opExtrude","SWEPT_EDGE",EDGE,{"disambiguationData":[OSD([subQ3,subQ2,subQ1,subQ0]),TDD([makeQuery(id+"F2.imprint","INTERSECT",VERTEX,{"disambiguationData":[OD(1.0)],"derivedFrom":[makeQuery(id+"F1.opExtrude","CAP_EDGE",EDGE,{"disambiguationData":[OSD([subQ3,subQ2])],"isStart":false}),subQ1,subQ0]})])]})});}
            var Q26;
            {var subQ0=sQuery(id+"F2.wireOp",EDGE,"E68.MirrorCS");var subQ1=sQuery(id+"F2.wireOp",EDGE,"E67.MirrorCS");var subQ2=sQuery(id+"F0.wireOp",EDGE,"E39.MirrorCS");var subQ3=sQuery(id+"F0.wireOp",EDGE,"E31.MirrorCS");Q26=makeQuery(id+"F3.boolean.opBoolean","COPY",EDGE,{"derivedFrom":makeQuery(id+"F3.opExtrude","SWEPT_EDGE",EDGE,{"disambiguationData":[OSD([subQ3,subQ2,subQ1,subQ0]),TDD([makeQuery(id+"F2.imprint","INTERSECT",VERTEX,{"disambiguationData":[OD(0.0)],"derivedFrom":[makeQuery(id+"F1.opExtrude","CAP_EDGE",EDGE,{"disambiguationData":[OSD([subQ3,subQ2])],"isStart":false}),subQ1,subQ0]})])]})});}
            var Q27;
            {var subQ0=sQuery(id+"F2.wireOp",EDGE,"E73.MirrorCS");var subQ1=sQuery(id+"F2.wireOp",EDGE,"E69.MirrorCS");var subQ2=sQuery(id+"F0.wireOp",EDGE,"E39.MirrorCS");var subQ3=sQuery(id+"F0.wireOp",EDGE,"E31.MirrorCS");Q27=makeQuery(id+"F3.boolean.opBoolean","COPY",EDGE,{"derivedFrom":makeQuery(id+"F3.opExtrude","SWEPT_EDGE",EDGE,{"disambiguationData":[OSD([subQ3,subQ2,subQ1,subQ0]),TDD([makeQuery(id+"F2.imprint","INTERSECT",VERTEX,{"disambiguationData":[OD(1.0)],"derivedFrom":[makeQuery(id+"F1.opExtrude","CAP_EDGE",EDGE,{"disambiguationData":[OSD([subQ3,subQ2])],"isStart":false}),subQ1,subQ0]})])]})});}
            var Q28;
            {var subQ0=sQuery(id+"F2.wireOp",EDGE,"E73.MirrorCS");var subQ1=sQuery(id+"F2.wireOp",EDGE,"E69.MirrorCS");var subQ2=sQuery(id+"F0.wireOp",EDGE,"E39.MirrorCS");var subQ3=sQuery(id+"F0.wireOp",EDGE,"E31.MirrorCS");Q28=makeQuery(id+"F3.boolean.opBoolean","COPY",EDGE,{"derivedFrom":makeQuery(id+"F3.opExtrude","SWEPT_EDGE",EDGE,{"disambiguationData":[OSD([subQ3,subQ2,subQ1,subQ0]),TDD([makeQuery(id+"F2.imprint","INTERSECT",VERTEX,{"disambiguationData":[OD(0.0)],"derivedFrom":[makeQuery(id+"F1.opExtrude","CAP_EDGE",EDGE,{"disambiguationData":[OSD([subQ3,subQ2])],"isStart":false}),subQ1,subQ0]})])]})});}
            var Q29;
            {var subQ0=sQuery(id+"F2.wireOp",EDGE,"E74.MirrorCS");var subQ1=sQuery(id+"F2.wireOp",EDGE,"E70.MirrorCS");var subQ2=sQuery(id+"F0.wireOp",EDGE,"E39.MirrorCS");var subQ3=sQuery(id+"F0.wireOp",EDGE,"E31.MirrorCS");Q29=makeQuery(id+"F3.boolean.opBoolean","COPY",EDGE,{"derivedFrom":makeQuery(id+"F3.opExtrude","SWEPT_EDGE",EDGE,{"disambiguationData":[OSD([subQ3,subQ2,subQ1,subQ0]),TDD([makeQuery(id+"F2.imprint","INTERSECT",VERTEX,{"disambiguationData":[OD(1.0)],"derivedFrom":[makeQuery(id+"F1.opExtrude","CAP_EDGE",EDGE,{"disambiguationData":[OSD([subQ3,subQ2])],"isStart":false}),subQ1,subQ0]})])]})});}
            var Q30;
            {var subQ0=sQuery(id+"F2.wireOp",EDGE,"E74.MirrorCS");var subQ1=sQuery(id+"F2.wireOp",EDGE,"E70.MirrorCS");var subQ2=sQuery(id+"F0.wireOp",EDGE,"E39.MirrorCS");var subQ3=sQuery(id+"F0.wireOp",EDGE,"E31.MirrorCS");Q30=makeQuery(id+"F3.boolean.opBoolean","COPY",EDGE,{"derivedFrom":makeQuery(id+"F3.opExtrude","SWEPT_EDGE",EDGE,{"disambiguationData":[OSD([subQ3,subQ2,subQ1,subQ0]),TDD([makeQuery(id+"F2.imprint","INTERSECT",VERTEX,{"disambiguationData":[OD(0.0)],"derivedFrom":[makeQuery(id+"F1.opExtrude","CAP_EDGE",EDGE,{"disambiguationData":[OSD([subQ3,subQ2])],"isStart":false}),subQ1,subQ0]})])]})});}
            var Q31;
            {var subQ0=sQuery(id+"F2.wireOp",EDGE,"E75.MirrorCS");var subQ1=sQuery(id+"F2.wireOp",EDGE,"E71.MirrorCS");var subQ2=sQuery(id+"F0.wireOp",EDGE,"E39.MirrorCS");var subQ3=sQuery(id+"F0.wireOp",EDGE,"E31.MirrorCS");Q31=makeQuery(id+"F3.boolean.opBoolean","COPY",EDGE,{"derivedFrom":makeQuery(id+"F3.opExtrude","SWEPT_EDGE",EDGE,{"disambiguationData":[OSD([subQ3,subQ2,subQ1,subQ0]),TDD([makeQuery(id+"F2.imprint","INTERSECT",VERTEX,{"disambiguationData":[OD(1.0)],"derivedFrom":[makeQuery(id+"F1.opExtrude","CAP_EDGE",EDGE,{"disambiguationData":[OSD([subQ3,subQ2])],"isStart":false}),subQ1,subQ0]})])]})});}
            var Q32;
            {var subQ0=sQuery(id+"F2.wireOp",EDGE,"E75.MirrorCS");var subQ1=sQuery(id+"F2.wireOp",EDGE,"E71.MirrorCS");var subQ2=sQuery(id+"F0.wireOp",EDGE,"E39.MirrorCS");var subQ3=sQuery(id+"F0.wireOp",EDGE,"E31.MirrorCS");Q32=makeQuery(id+"F3.boolean.opBoolean","COPY",EDGE,{"derivedFrom":makeQuery(id+"F3.opExtrude","SWEPT_EDGE",EDGE,{"disambiguationData":[OSD([subQ3,subQ2,subQ1,subQ0]),TDD([makeQuery(id+"F2.imprint","INTERSECT",VERTEX,{"disambiguationData":[OD(0.0)],"derivedFrom":[makeQuery(id+"F1.opExtrude","CAP_EDGE",EDGE,{"disambiguationData":[OSD([subQ3,subQ2])],"isStart":false}),subQ1,subQ0]})])]})});}
            var Q33;
            {var subQ0=sQuery(id+"F2.wireOp",EDGE,"E76.MirrorCS");var subQ1=sQuery(id+"F2.wireOp",EDGE,"E72.MirrorCS");var subQ2=sQuery(id+"F0.wireOp",EDGE,"E39.MirrorCS");var subQ3=sQuery(id+"F0.wireOp",EDGE,"E31.MirrorCS");Q33=makeQuery(id+"F3.boolean.opBoolean","COPY",EDGE,{"derivedFrom":makeQuery(id+"F3.opExtrude","SWEPT_EDGE",EDGE,{"disambiguationData":[OSD([subQ3,subQ2,subQ1,subQ0]),TDD([makeQuery(id+"F2.imprint","INTERSECT",VERTEX,{"disambiguationData":[OD(0.0)],"derivedFrom":[makeQuery(id+"F1.opExtrude","CAP_EDGE",EDGE,{"disambiguationData":[OSD([subQ3,subQ2])],"isStart":false}),subQ1,subQ0]})])]})});}
            var Q34;
            {var subQ0=sQuery(id+"F2.wireOp",EDGE,"E76.MirrorCS");var subQ1=sQuery(id+"F2.wireOp",EDGE,"E72.MirrorCS");var subQ2=sQuery(id+"F0.wireOp",EDGE,"E39.MirrorCS");var subQ3=sQuery(id+"F0.wireOp",EDGE,"E31.MirrorCS");Q34=makeQuery(id+"F3.boolean.opBoolean","COPY",EDGE,{"derivedFrom":makeQuery(id+"F3.opExtrude","SWEPT_EDGE",EDGE,{"disambiguationData":[OSD([subQ3,subQ2,subQ1,subQ0]),TDD([makeQuery(id+"F2.imprint","INTERSECT",VERTEX,{"disambiguationData":[OD(1.0)],"derivedFrom":[makeQuery(id+"F1.opExtrude","CAP_EDGE",EDGE,{"disambiguationData":[OSD([subQ3,subQ2])],"isStart":false}),subQ1,subQ0]})])]})});}
            fillet(context, id + "F4", {"entities" : qUnion([Q0, Q1, Q2, Q3, Q4, Q5, Q6, Q7, Q8, Q9, Q10, Q11, Q12, Q13, Q14, Q15, Q16, Q17, Q18, Q19, Q20, Q21, Q22, Q23, Q24, Q25, Q26, Q27, Q28, Q29, Q30, Q31, Q32, Q33, Q34]), "radius" : 2.03 * mm, "tangentPropagation" : true, "allowEdgeOverflow" : false});
        }
    });
